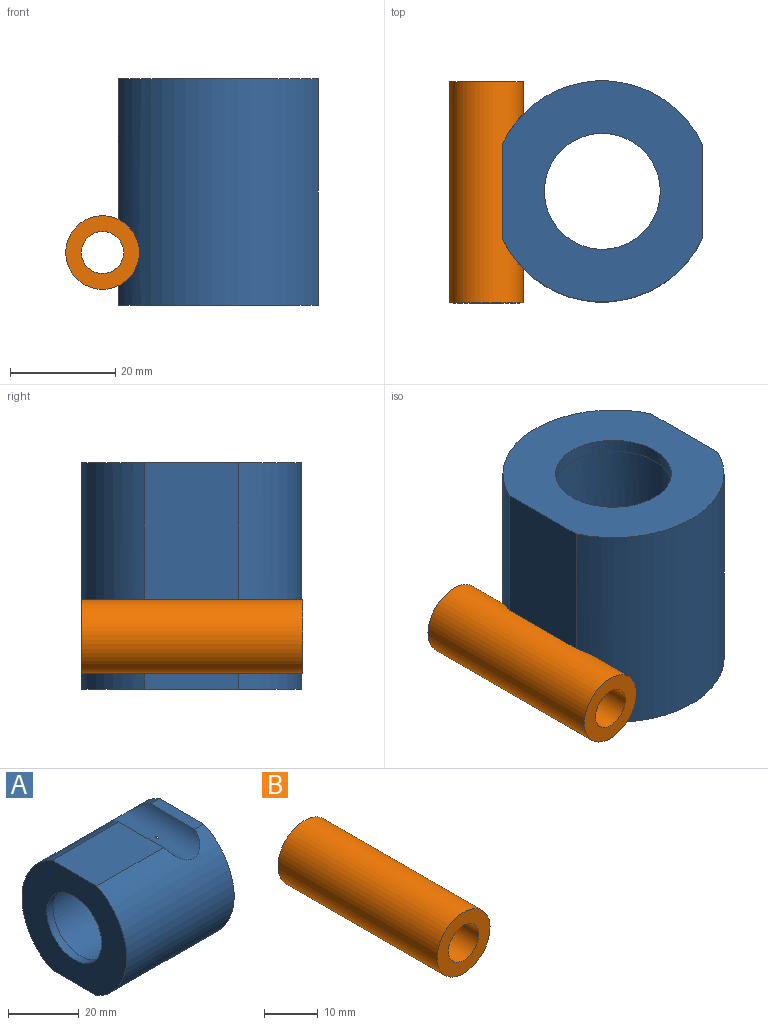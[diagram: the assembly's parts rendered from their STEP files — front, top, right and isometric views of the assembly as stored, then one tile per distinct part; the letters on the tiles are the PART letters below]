
ASSEMBLY  parts=2 mates=1
PART A: 15 faces, bbox 43x42x38 mm
  f0: plane 17.89x3.67mm, normal (0,0,1), area 65.7mm2, adj f1,f2,f3,f14
  f1: plane 42x38mm, normal (1,0,0), area 533mm2, adj f0,f2,f3,f11,f12
  f2: cylinder r=21mm len=43mm, axis (-1,0,0), area 1975.5mm2, adj f0,f1,f4,f12,f13,f14
  f3: cylinder r=21mm len=43mm, axis (-1,0,0), area 1975.6mm2, adj f0,f1,f4,f12,f13,f14
  f4: plane 42x38mm, normal (-1,0,0), area 957.1mm2, adj f2,f3,f7,f12,f13
  f5: plane 30x30mm, normal (1,0,0), area 134.3mm2, adj f6,f10
  f6: cylinder r=15mm len=30mm, axis (-1,0,0), area 2308.4mm2, adj f5,f11,f14
  f7: cylinder r=11mm len=22mm, axis (-1,0,0), area 172.8mm2, adj f4,f8
  f8: plane 25x25mm, normal (1,0,0), area 110.7mm2, adj f7,f9
  f9: cylinder r=12.5mm len=25mm, axis (-1,0,0), area 1099.6mm2, adj f8,f10
  f10: cone r=13.5mm half-angle=45deg, axis (1,0,0), area 115.5mm2, adj f5,f9
  f11: cone r=16mm half-angle=45deg, axis (1,0,0), area 137.7mm2, adj f1,f6
  f12: plane 43x17.89mm, normal (0,0,-1), area 769.2mm2, adj f1,f2,f3,f4
  f13: plane 26.67x17.89mm, normal (0,0,1), area 477.1mm2, adj f2,f3,f4,f14
  f14: cylinder r=7mm len=29.42mm, axis (0,-1,0), area 409.6mm2, adj f0,f2,f3,f6,f13
PART B: 4 faces, bbox 14x42x14 mm
  f0: cylinder r=4mm len=42mm, axis (0,1,0), area 1055.6mm2, adj f2,f3
  f1: cylinder r=7mm len=42mm, axis (0,1,0), area 1847.3mm2, adj f2,f3
  f2: plane 14x14mm, normal (0,-1,0), area 103.7mm2, adj f0,f1
  f3: plane 14x14mm, normal (0,1,0), area 103.7mm2, adj f0,f1
PLACE A rot(axis=(0.71,0,-0.71),180deg) t=(25.85,4.27,33.98)mm
PLACE B rot(axis=(0,0,1),180deg) t=(3.86,4.11,0.98)mm
MATE cylindrical A.f14 <-> B.f1  axis (0,1,0) through (3.86,19.17,0.98)mm
